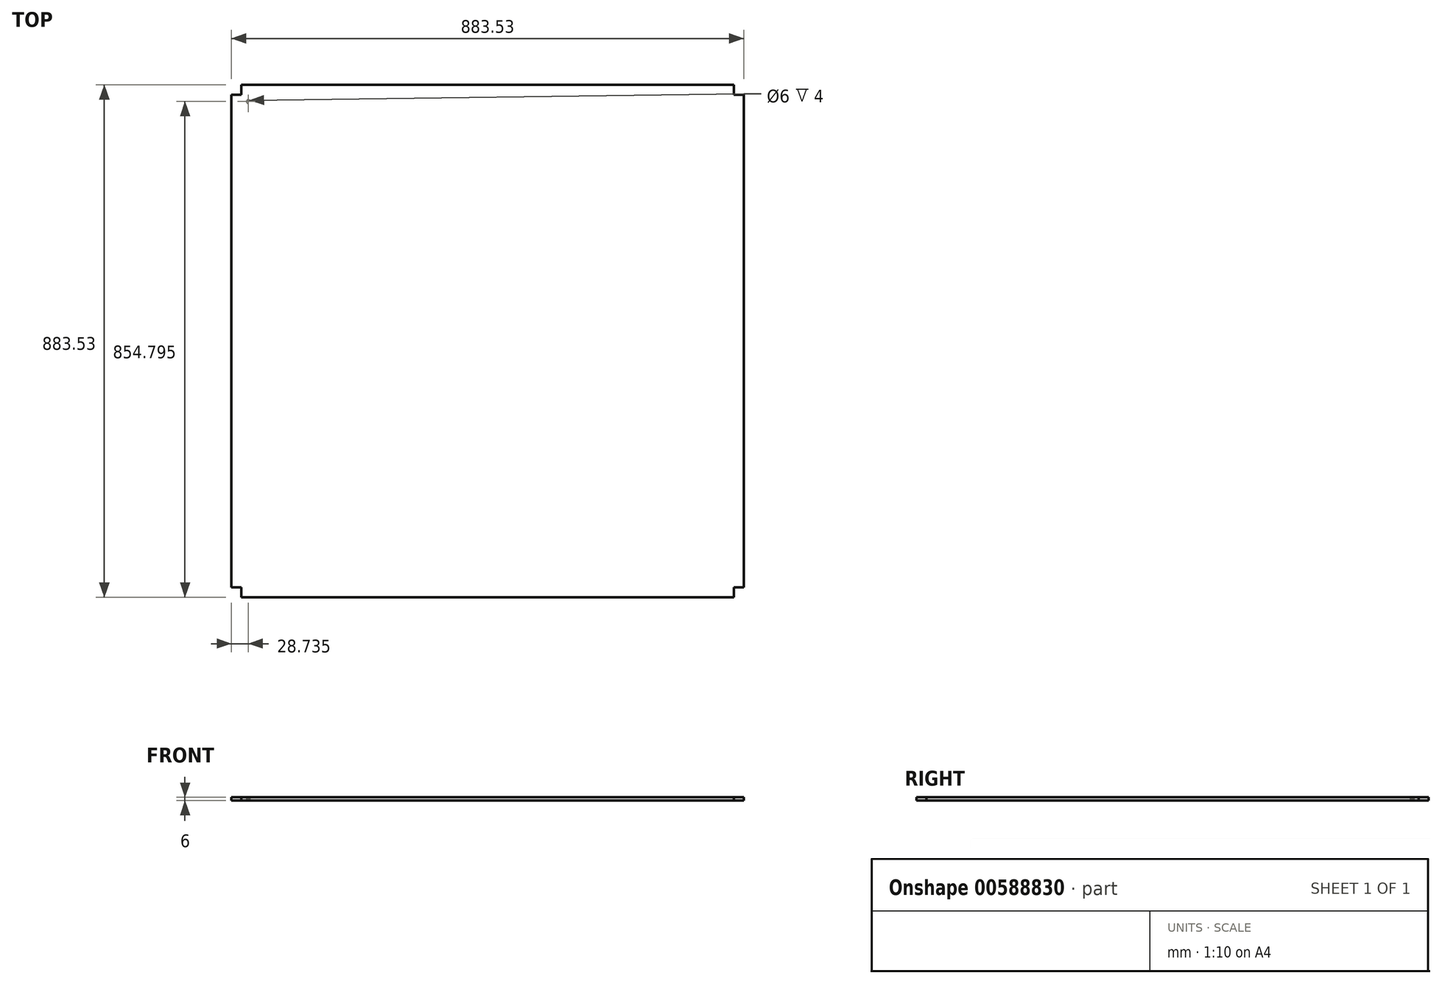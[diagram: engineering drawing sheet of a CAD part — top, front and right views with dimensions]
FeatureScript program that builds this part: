
annotation { "Feature Type Name" : "Feature", "Feature Type Description" : "" }
export const myFeature = defineFeature(function(context is Context, id is Id, definition is map)
    precondition{}
    {
        {
            var Q0;
            Q0=qCreatedBy(makeId("Front.planeOp"),FACE);
            var sketch = newSketch(context, id + "F0", { "sketchPlane" : qUnion([Q0])});
            skLineSegment(sketch, "E0.bottom", {"start": v(0, 0) * mm, "end": v(883.53, 0) * mm});
            skLineSegment(sketch, "E0.top", {"start": v(0, 6) * mm, "end": v(883.53, 6) * mm});
            skLineSegment(sketch, "E0.left", {"start": v(0, 0) * mm, "end": v(0, 6) * mm});
            skLineSegment(sketch, "E0.right", {"start": v(883.53, 0) * mm, "end": v(883.53, 6) * mm});
            skSolve(sketch);
        }
        {
            var Q0;
            Q0=makeQuery(id+"F0.imprint","IMPRINT",FACE,{"disambiguationData":[TD([[makeQuery(id+"F0.imprint","IMPRINT",EDGE,{"derivedFrom":sQuery(id+"F0.wireOp",EDGE,"E0.bottom")}),1.0]])]});
            extrude(context, id + "F1", {"entities" : qUnion([Q0]), "depth" : 883.53 * mm, "offsetDistance" : 25 * mm});
        }
        {
            var Q0;
            Q0=makeQuery(id+"F1.opExtrude","SWEPT_FACE",FACE,{"disambiguationData":[OSD([sQuery(id+"F0.wireOp",EDGE,"E0.top")])]});
            var sketch = newSketch(context, id + "F2", { "sketchPlane" : qUnion([Q0])});
            skLineSegment(sketch, "E1.bottom", {"start": v(0, 0) * mm, "end": v(17, 0) * mm});
            skLineSegment(sketch, "E1.top", {"start": v(0, -17) * mm, "end": v(17, -17) * mm});
            skLineSegment(sketch, "E1.left", {"start": v(0, 0) * mm, "end": v(0, -17) * mm});
            skLineSegment(sketch, "E1.right", {"start": v(17, 0) * mm, "end": v(17, -17) * mm});
            skSolve(sketch);
        }
        {
            var Q0;
            Q0=makeQuery(id+"F2.imprint","IMPRINT",FACE,{"disambiguationData":[TD([[makeQuery(id+"F2.imprint","IMPRINT",EDGE,{"derivedFrom":sQuery(id+"F2.wireOp",EDGE,"E1.bottom")}),-1.0]])]});
            extrude(context, id + "F3", {"entities" : qUnion([Q0]), "operationType" : NewBodyOperationType.REMOVE, "oppositeDirection" : true, "depth" : 6 * mm, "offsetDistance" : 25 * mm});
        }
        {
            var Q0;
            Q0=makeQuery(id+"F1.opExtrude","SWEPT_FACE",FACE,{"disambiguationData":[OSD([sQuery(id+"F0.wireOp",EDGE,"E0.top")])]});
            var sketch = newSketch(context, id + "F4", { "sketchPlane" : qUnion([Q0])});
            skLineSegment(sketch, "E2.bottom", {"start": v(883.53, 0) * mm, "end": v(866.53, 0) * mm});
            skLineSegment(sketch, "E2.top", {"start": v(883.53, -17) * mm, "end": v(866.53, -17) * mm});
            skLineSegment(sketch, "E2.left", {"start": v(883.53, 0) * mm, "end": v(883.53, -17) * mm});
            skLineSegment(sketch, "E2.right", {"start": v(866.53, 0) * mm, "end": v(866.53, -17) * mm});
            skSolve(sketch);
        }
        {
            var Q0;
            Q0=makeQuery(id+"F4.imprint","IMPRINT",FACE,{"disambiguationData":[TD([[makeQuery(id+"F4.imprint","IMPRINT",EDGE,{"derivedFrom":sQuery(id+"F4.wireOp",EDGE,"E2.bottom")}),-1.0]])]});
            extrude(context, id + "F5", {"entities" : qUnion([Q0]), "operationType" : NewBodyOperationType.REMOVE, "oppositeDirection" : true, "depth" : 6 * mm, "offsetDistance" : 25 * mm});
        }
        {
            var Q0;
            Q0=makeQuery(id+"F1.opExtrude","SWEPT_FACE",FACE,{"disambiguationData":[OSD([sQuery(id+"F0.wireOp",EDGE,"E0.top")])]});
            var sketch = newSketch(context, id + "F6", { "sketchPlane" : qUnion([Q0])});
            skLineSegment(sketch, "E3.bottom", {"start": v(883.53, -883.53) * mm, "end": v(866.53, -883.53) * mm});
            skLineSegment(sketch, "E3.top", {"start": v(883.53, -866.53) * mm, "end": v(866.53, -866.53) * mm});
            skLineSegment(sketch, "E3.left", {"start": v(883.53, -883.53) * mm, "end": v(883.53, -866.53) * mm});
            skLineSegment(sketch, "E3.right", {"start": v(866.53, -883.53) * mm, "end": v(866.53, -866.53) * mm});
            skSolve(sketch);
        }
        {
            var Q0;
            Q0=makeQuery(id+"F6.imprint","IMPRINT",FACE,{"disambiguationData":[TD([[makeQuery(id+"F6.imprint","IMPRINT",EDGE,{"derivedFrom":sQuery(id+"F6.wireOp",EDGE,"E3.bottom")}),1.0]])]});
            extrude(context, id + "F7", {"entities" : qUnion([Q0]), "operationType" : NewBodyOperationType.REMOVE, "oppositeDirection" : true, "depth" : 6 * mm, "offsetDistance" : 25 * mm});
        }
        {
            var Q0;
            Q0=makeQuery(id+"F1.opExtrude","SWEPT_FACE",FACE,{"disambiguationData":[OSD([sQuery(id+"F0.wireOp",EDGE,"E0.top")])]});
            var sketch = newSketch(context, id + "F8", { "sketchPlane" : qUnion([Q0])});
            skLineSegment(sketch, "E4.bottom", {"start": v(0, -883.53) * mm, "end": v(17, -883.53) * mm});
            skLineSegment(sketch, "E4.top", {"start": v(0, -866.53) * mm, "end": v(17, -866.53) * mm});
            skLineSegment(sketch, "E4.left", {"start": v(0, -883.53) * mm, "end": v(0, -866.53) * mm});
            skLineSegment(sketch, "E4.right", {"start": v(17, -883.53) * mm, "end": v(17, -866.53) * mm});
            skSolve(sketch);
        }
        {
            var Q0;
            Q0=makeQuery(id+"F8.imprint","IMPRINT",FACE,{"disambiguationData":[TD([[makeQuery(id+"F8.imprint","IMPRINT",EDGE,{"derivedFrom":sQuery(id+"F8.wireOp",EDGE,"E4.bottom")}),1.0]])]});
            extrude(context, id + "F9", {"entities" : qUnion([Q0]), "operationType" : NewBodyOperationType.REMOVE, "oppositeDirection" : true, "depth" : 6 * mm, "offsetDistance" : 25 * mm});
        }
        {
            var Q0;
            Q0=makeQuery(id+"F1.opExtrude","SWEPT_FACE",FACE,{"disambiguationData":[OSD([sQuery(id+"F0.wireOp",EDGE,"E0.bottom")])]});
            var sketch = newSketch(context, id + "F10", { "sketchPlane" : qUnion([Q0])});
            skCircle(sketch, "E5", {"center": v(28.73, 28.73) * mm, "radius": 3 * mm});
            skSolve(sketch);
        }
        {
            var Q0;
            Q0=makeQuery(id+"F10.imprint","IMPRINT",FACE,{"disambiguationData":[TD([[makeQuery(id+"F10.imprint","IMPRINT",EDGE,{"derivedFrom":sQuery(id+"F10.wireOp",EDGE,"E5")}),1.0]])]});
            extrude(context, id + "F11", {"entities" : qUnion([Q0]), "operationType" : NewBodyOperationType.REMOVE, "oppositeDirection" : true, "depth" : 4 * mm, "offsetDistance" : 25 * mm});
        }
    });
